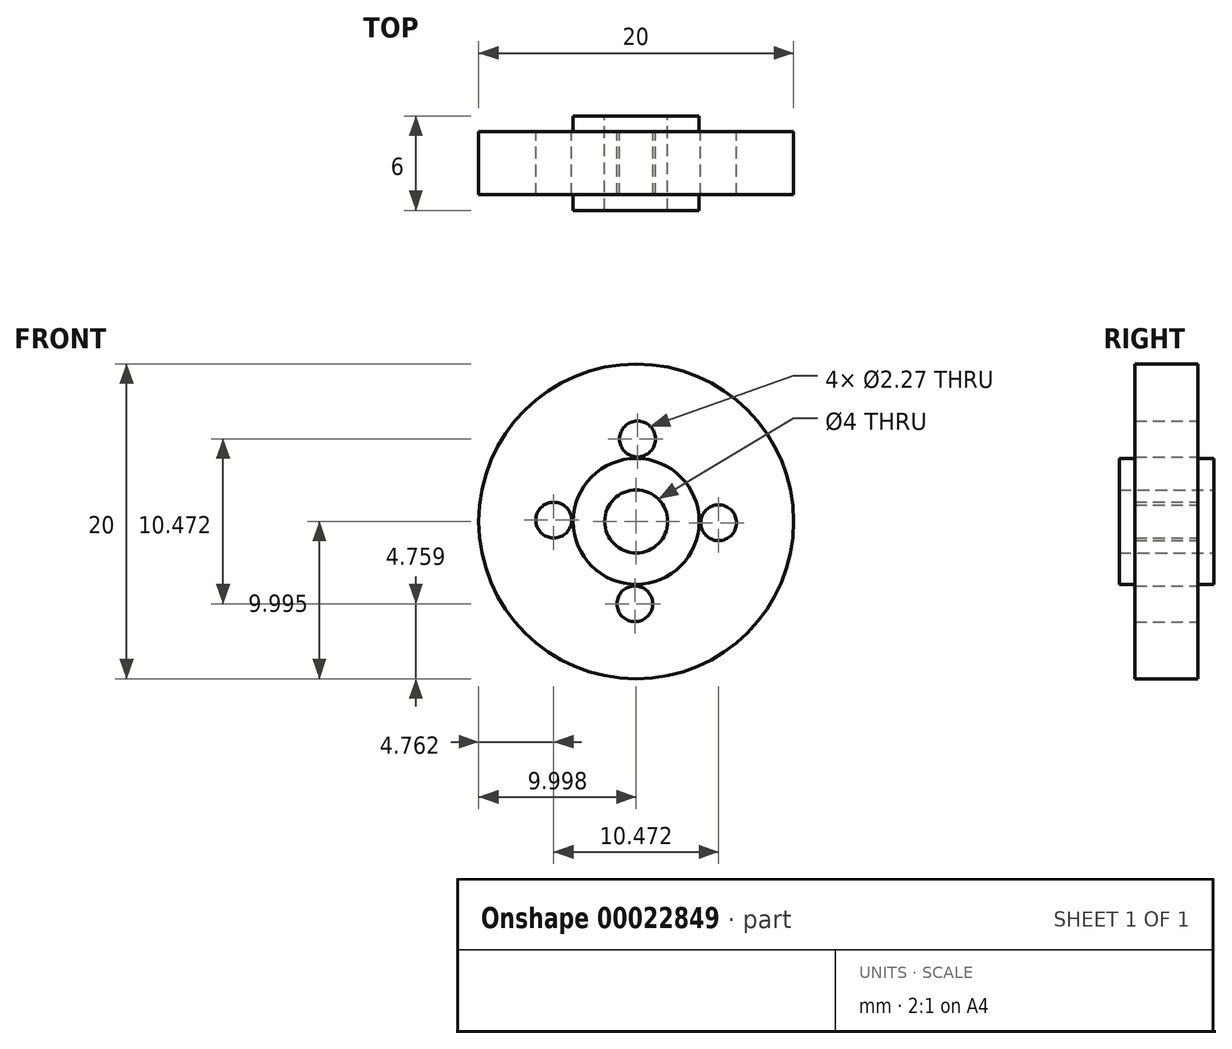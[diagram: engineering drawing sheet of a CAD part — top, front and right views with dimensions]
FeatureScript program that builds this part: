
annotation { "Feature Type Name" : "Feature", "Feature Type Description" : "" }
export const myFeature = defineFeature(function(context is Context, id is Id, definition is map)
    precondition{}
    {
        {
            var Q0;
            Q0=qCreatedBy(makeId("Front.planeOp"),FACE);
            var sketch = newSketch(context, id + "F0", { "sketchPlane" : qUnion([Q0])});
            skCircle(sketch, "E0", {"center": v(-34.04, 11.93) * mm, "radius": 10 * mm});
            skCircle(sketch, "E1", {"center": v(-34.04, 11.93) * mm, "radius": 2 * mm});
            skCircle(sketch, "E2", {"center": v(-33.96, 17.16) * mm, "radius": 1.14 * mm});
            skCircle(sketch, "E3.1.0", {"center": v(-39.28, 12) * mm, "radius": 1.14 * mm});
            skCircle(sketch, "E3.2.0", {"center": v(-34.13, 6.69) * mm, "radius": 1.14 * mm});
            skCircle(sketch, "E3.3.0", {"center": v(-28.8, 11.84) * mm, "radius": 1.14 * mm});
            skCircle(sketch, "E4", {"center": v(-34.04, 11.93) * mm, "radius": 4 * mm});
            skSolve(sketch);
        }
        {
            var Q0;
            Q0 = qSketchRegion(id + "F0", true);
            extrude(context, id + "F1", {"entities" : qUnion([Q0]), "endBound" : BoundingType.SYMMETRIC, "depth" : 4 * mm});
        }
        {
            var Q0;
            Q0=makeQuery(id+"F0.imprint","IMPRINT",FACE,{"disambiguationData":[TD([[makeQuery(id+"F0.imprint","IMPRINT",EDGE,{"derivedFrom":sQuery(id+"F0.wireOp",EDGE,"E1")}),-1.0]])]});
            extrude(context, id + "F2", {"entities" : qUnion([Q0]), "operationType" : NewBodyOperationType.ADD, "endBound" : BoundingType.SYMMETRIC, "depth" : 6 * mm});
        }
    });
